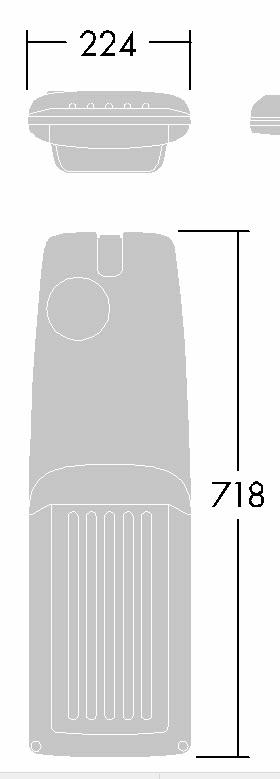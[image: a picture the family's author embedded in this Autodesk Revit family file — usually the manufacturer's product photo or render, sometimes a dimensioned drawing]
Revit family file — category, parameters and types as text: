
# Revit family: Thorn ISARO PRO Medium top entry 60mm
name_source: partatom
category: Lighting Fixtures
revit_build: Autodesk Revit 2016 (Build: 20150220_1215(x64)
units: mm (PartAtom-declared; Revit-internal decimal feet)

## family parameters
Always vertical = Yes
Cut with Voids When Loaded = No
Light Source = Yes
OmniClass Number = 23.80.70.14
OmniClass Title = Luminaries for External Lighting
Part Type = Normal
Room Calculation Point = No
Round Connector Dimension = Use Diameter
Shared = No
Work Plane-Based = Yes

## types (1)
- Isaro PRO Medium top entry 60mm
    Apparent Load = 89 VA
    Color Filter = 16777215
    Default Elevation = 0 mm  [stored 0 ft]
    Description = LED road lighting luminaire
    Dimming Lamp Color Temperature Shift = <None>
    Emit Shape Visible in Rendering = No
    Emit from Rectangle Length = 374 mm  [stored 1.22703 ft]
    Emit from Rectangle Width = 194 mm  [stored 0.636483 ft]
    Height = 114 mm  [stored 0.374016 ft]
    Lamp = LED
    Length = 718 mm  [stored 2.35564 ft]
    Manufacturer = Thorn Lighting
    Model = 96276047
    Photometric Web File = 96276047_(STD).IES
    Tilt Angle = 90.00°
    URL = www.thornlighting.com/96276047
    Voltage = 230 V
    Width = 224 mm  [stored 0.734908 ft]

note: [stored X ft] marks values corroborated as IEEE doubles in the binary element streams (Revit-internal decimal feet)

## geometry (parser evidence)
native form markers: Sweep x7
no freeform markers — native parametric forms only
